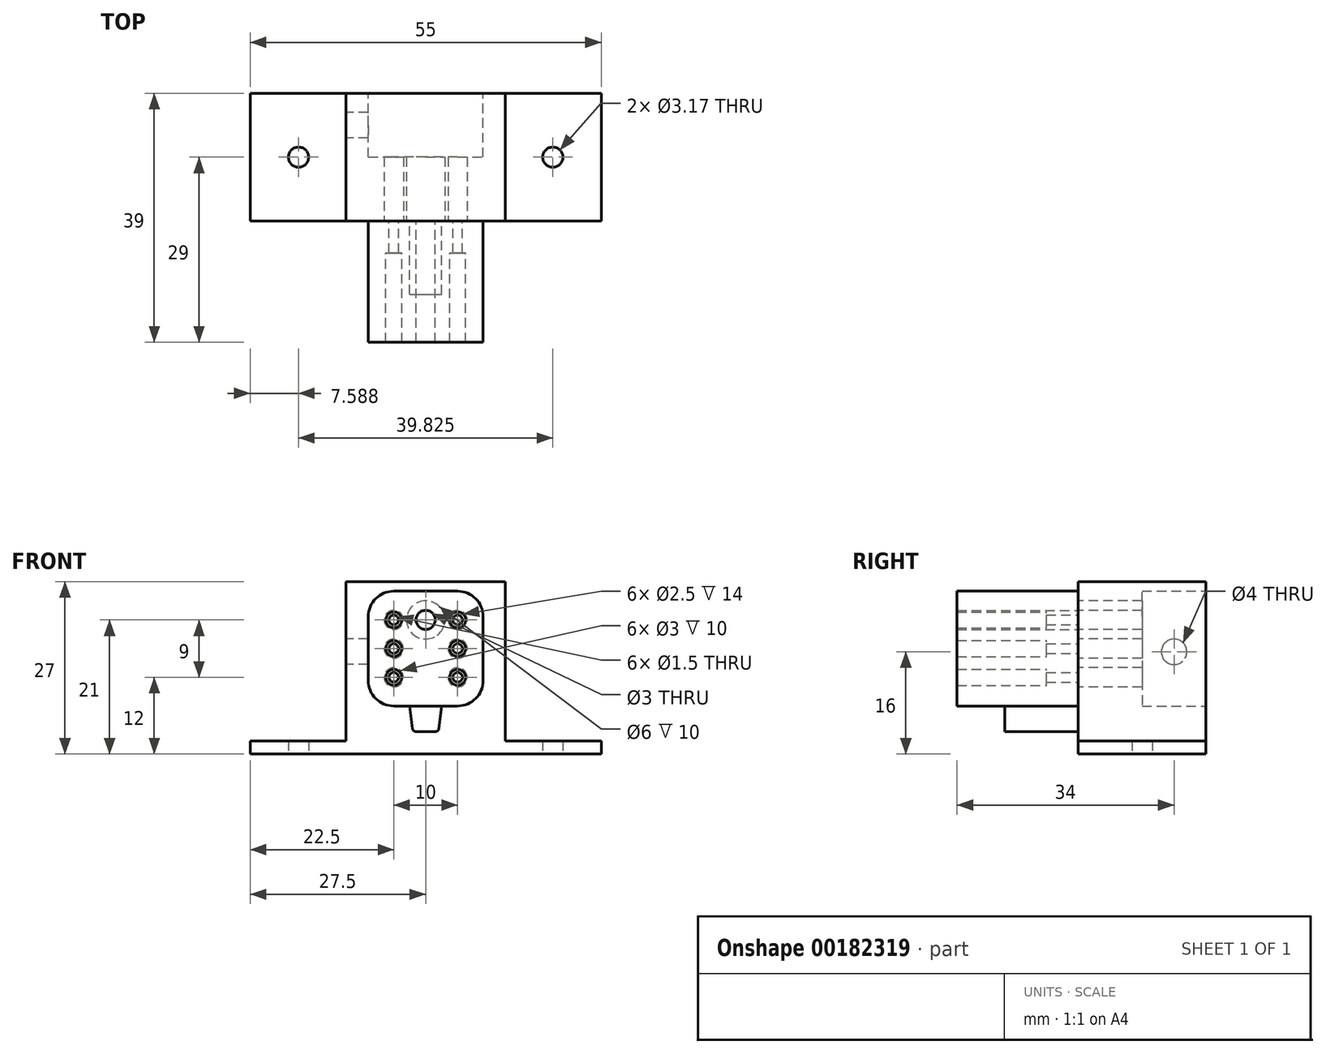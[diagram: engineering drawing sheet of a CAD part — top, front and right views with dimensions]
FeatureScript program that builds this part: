
annotation { "Feature Type Name" : "Feature", "Feature Type Description" : "" }
export const myFeature = defineFeature(function(context is Context, id is Id, definition is map)
    precondition{}
    {
        {
            var Q0;
            Q0=qCreatedBy(makeId("Top.planeOp"),FACE);
            var sketch = newSketch(context, id + "F0", { "sketchPlane" : qUnion([Q0])});
            skLineSegment(sketch, "E0.bottom", {"start": v(0, 0) * mm, "end": v(25, 0) * mm});
            skLineSegment(sketch, "E0.top", {"start": v(0, 20) * mm, "end": v(25, 20) * mm});
            skLineSegment(sketch, "E0.left", {"start": v(0, 0) * mm, "end": v(0, 20) * mm});
            skLineSegment(sketch, "E0.right", {"start": v(25, 0) * mm, "end": v(25, 20) * mm});
            skSolve(sketch);
        }
        {
            var Q0;
            Q0 = qSketchRegion(id + "F0", true);
            extrude(context, id + "F1", {"entities" : qUnion([Q0]), "depth" : 32 * mm});
        }
        {
            var Q0;
            Q0=makeQuery(id+"F1.opExtrude","SWEPT_FACE",FACE,{"disambiguationData":[OSD([sQuery(id+"F0.wireOp",EDGE,"E0.bottom")])]});
            var sketch = newSketch(context, id + "F2", { "sketchPlane" : qUnion([Q0])});
            skLineSegment(sketch, "E1.bottom", {"start": v(7.5, 30.5) * mm, "end": v(17.5, 30.5) * mm});
            skLineSegment(sketch, "E1.top", {"start": v(7.5, 12.5) * mm, "end": v(17.5, 12.5) * mm});
            skLineSegment(sketch, "E1.left", {"start": v(3.5, 26.5) * mm, "end": v(3.5, 16.5) * mm});
            skLineSegment(sketch, "E1.right", {"start": v(21.5, 26.5) * mm, "end": v(21.5, 16.5) * mm});
            skLineSegment(sketch, "E2", {"start": v(3.5, 21.5) * mm, "end": v(0, 21.5) * mm, "construction": true});
            skLineSegment(sketch, "E3", {"start": v(21.5, 21.5) * mm, "end": v(25, 21.5) * mm, "construction": true});
            skPoint(sketch, "E4.visualSharp", {"position": v(3.5, 30.5) * mm});
            skArc(sketch, "E4.filletArc", {"start": v(7.5, 30.5) * mm, "mid": v(4.67, 29.33) * mm, "end": v(3.5, 26.5) * mm});
            skPoint(sketch, "E5.visualSharp", {"position": v(21.5, 30.5) * mm});
            skArc(sketch, "E5.filletArc", {"start": v(21.5, 26.5) * mm, "mid": v(20.33, 29.33) * mm, "end": v(17.5, 30.5) * mm});
            skPoint(sketch, "E6.visualSharp", {"position": v(21.5, 12.5) * mm});
            skArc(sketch, "E6.filletArc", {"start": v(17.5, 12.5) * mm, "mid": v(20.33, 13.67) * mm, "end": v(21.5, 16.5) * mm});
            skPoint(sketch, "E7.visualSharp", {"position": v(3.5, 12.5) * mm});
            skArc(sketch, "E7.filletArc", {"start": v(3.5, 16.5) * mm, "mid": v(4.67, 13.67) * mm, "end": v(7.5, 12.5) * mm});
            skLineSegment(sketch, "E8", {"start": v(12.5, 30.5) * mm, "end": v(12.5, 6.08) * mm, "construction": true});
            skCircle(sketch, "E9", {"center": v(12.5, 26) * mm, "radius": 1.5 * mm});
            skCircle(sketch, "E10", {"center": v(7.5, 26) * mm, "radius": 1.25 * mm});
            skLineSegment(sketch, "E11", {"start": v(7.5, 26) * mm, "end": v(12.5, 26) * mm, "construction": true});
            skCircle(sketch, "E12.1.0.0", {"center": v(7.5, 21.5) * mm, "radius": 1.25 * mm});
            skCircle(sketch, "E12.2.0.0", {"center": v(7.5, 17) * mm, "radius": 1.25 * mm});
            skLineSegment(sketch, "E12.direction1", {"start": v(7.5, 26) * mm, "end": v(7.5, 21.5) * mm, "construction": true});
            skCircle(sketch, "E13.MirrorC", {"center": v(17.5, 26) * mm, "radius": 1.25 * mm});
            skCircle(sketch, "E14.MirrorC", {"center": v(17.5, 21.5) * mm, "radius": 1.25 * mm});
            skCircle(sketch, "E15.MirrorC", {"center": v(17.5, 17) * mm, "radius": 1.25 * mm});
            skLineSegment(sketch, "E16.MirrorCS", {"start": v(17.5, 26) * mm, "end": v(17.5, 21.5) * mm, "construction": true});
            skSolve(sketch);
        }
        {
            var Q0;
            Q0 = qSketchRegion(id + "F2", true);
            extrude(context, id + "F3", {"entities" : qUnion([Q0]), "operationType" : NewBodyOperationType.ADD, "depth" : 19 * mm});
        }
        {
            var Q0;
            Q0=makeQuery(id+"F1.opExtrude","SWEPT_FACE",FACE,{"disambiguationData":[OSD([sQuery(id+"F0.wireOp",EDGE,"E0.top")])]});
            var sketch = newSketch(context, id + "F4", { "sketchPlane" : qUnion([Q0])});
            skLineSegment(sketch, "E17.bottom", {"start": v(-17.5, 30.5) * mm, "end": v(-7.5, 30.5) * mm});
            skLineSegment(sketch, "E17.top", {"start": v(-17.5, 12.5) * mm, "end": v(-7.5, 12.5) * mm});
            skLineSegment(sketch, "E17.left", {"start": v(-21.5, 26.5) * mm, "end": v(-21.5, 16.5) * mm});
            skLineSegment(sketch, "E17.right", {"start": v(-3.5, 26.5) * mm, "end": v(-3.5, 16.5) * mm});
            skLineSegment(sketch, "E18", {"start": v(-21.5, 21.5) * mm, "end": v(-25, 21.5) * mm, "construction": true});
            skLineSegment(sketch, "E19", {"start": v(-3.5, 21.5) * mm, "end": v(0, 21.5) * mm, "construction": true});
            skPoint(sketch, "E20.visualSharp", {"position": v(-21.5, 30.5) * mm});
            skArc(sketch, "E20.filletArc", {"start": v(-17.5, 30.5) * mm, "mid": v(-20.33, 29.33) * mm, "end": v(-21.5, 26.5) * mm});
            skPoint(sketch, "E21.visualSharp", {"position": v(-3.5, 30.5) * mm});
            skArc(sketch, "E21.filletArc", {"start": v(-3.5, 26.5) * mm, "mid": v(-4.67, 29.33) * mm, "end": v(-7.5, 30.5) * mm});
            skPoint(sketch, "E22.visualSharp", {"position": v(-3.5, 12.5) * mm});
            skArc(sketch, "E22.filletArc", {"start": v(-7.5, 12.5) * mm, "mid": v(-4.67, 13.67) * mm, "end": v(-3.5, 16.5) * mm});
            skPoint(sketch, "E23.visualSharp", {"position": v(-21.5, 12.5) * mm});
            skArc(sketch, "E23.filletArc", {"start": v(-21.5, 16.5) * mm, "mid": v(-20.33, 13.67) * mm, "end": v(-17.5, 12.5) * mm});
            skSolve(sketch);
        }
        {
            var Q0;
            Q0 = qSketchRegion(id + "F4", true);
            extrude(context, id + "F5", {"entities" : qUnion([Q0]), "operationType" : NewBodyOperationType.REMOVE, "oppositeDirection" : true, "depth" : 10 * mm});
        }
        {
            var Q0;
            Q0=makeQuery(id+"F1.opExtrude","SWEPT_FACE",FACE,{"disambiguationData":[OSD([sQuery(id+"F0.wireOp",EDGE,"E0.bottom")])]});
            var sketch = newSketch(context, id + "F6", { "sketchPlane" : qUnion([Q0])});
            skLineSegment(sketch, "E24.bottom", {"start": v(10, 12.5) * mm, "end": v(15, 12.5) * mm});
            skPoint(sketch, "E25", {"position": v(12.5, 12.5) * mm});
            skLineSegment(sketch, "E26", {"start": v(10, 12.5) * mm, "end": v(10.45, 8.94) * mm});
            skLineSegment(sketch, "E27", {"start": v(10.94, 8.5) * mm, "end": v(14.06, 8.5) * mm});
            skLineSegment(sketch, "E28", {"start": v(14.55, 8.94) * mm, "end": v(15, 12.5) * mm});
            skLineSegment(sketch, "E29", {"start": v(12.5, 8.5) * mm, "end": v(12.5, 12.5) * mm, "construction": true});
            skPoint(sketch, "E30.visualSharp", {"position": v(10.5, 8.5) * mm});
            skArc(sketch, "E30.filletArc", {"start": v(10.45, 8.94) * mm, "mid": v(10.61, 8.63) * mm, "end": v(10.94, 8.5) * mm});
            skPoint(sketch, "E31.visualSharp", {"position": v(14.5, 8.5) * mm});
            skArc(sketch, "E31.filletArc", {"start": v(14.06, 8.5) * mm, "mid": v(14.39, 8.63) * mm, "end": v(14.55, 8.94) * mm});
            skSolve(sketch);
        }
        {
            var Q0;
            Q0 = qSketchRegion(id + "F6", true);
            extrude(context, id + "F7", {"entities" : qUnion([Q0]), "operationType" : NewBodyOperationType.ADD, "depth" : 11.5 * mm});
        }
        {
            var Q0;
            Q0=makeQuery(id+"F1.opExtrude","SWEPT_FACE",FACE,{"disambiguationData":[OSD([sQuery(id+"F0.wireOp",EDGE,"E0.bottom")])]});
            var sketch = newSketch(context, id + "F8", { "sketchPlane" : qUnion([Q0])});
            skLineSegment(sketch, "E32", {"start": v(12.5, 30.5) * mm, "end": v(12.5, 12.5) * mm, "construction": true});
            skCircle(sketch, "E33", {"center": v(12.5, 26) * mm, "radius": 3 * mm});
            skCircle(sketch, "E34", {"center": v(7.5, 26) * mm, "radius": 1.5 * mm});
            skLineSegment(sketch, "E35", {"start": v(7.5, 26) * mm, "end": v(12.5, 26) * mm, "construction": true});
            skCircle(sketch, "E36.1.0.0", {"center": v(7.5, 21.5) * mm, "radius": 1.5 * mm});
            skCircle(sketch, "E36.2.0.0", {"center": v(7.5, 17) * mm, "radius": 1.5 * mm});
            skLineSegment(sketch, "E36.direction1", {"start": v(7.5, 26) * mm, "end": v(7.5, 21.5) * mm, "construction": true});
            skCircle(sketch, "E37.MirrorC", {"center": v(17.5, 26) * mm, "radius": 1.5 * mm});
            skCircle(sketch, "E38.MirrorC", {"center": v(17.5, 21.5) * mm, "radius": 1.5 * mm});
            skCircle(sketch, "E39.MirrorC", {"center": v(17.5, 17) * mm, "radius": 1.5 * mm});
            skLineSegment(sketch, "E40.MirrorCS", {"start": v(17.5, 26) * mm, "end": v(17.5, 21.5) * mm, "construction": true});
            skSolve(sketch);
        }
        {
            var Q0;
            Q0 = qSketchRegion(id + "F8", true);
            extrude(context, id + "F9", {"entities" : qUnion([Q0]), "operationType" : NewBodyOperationType.REMOVE, "endBound" : BoundingType.THROUGH_ALL, "oppositeDirection" : true, "depth" : 25 * mm});
        }
        {
            var Q0;
            Q0=makeQuery(id+"F1.opExtrude","SWEPT_FACE",FACE,{"disambiguationData":[OSD([sQuery(id+"F0.wireOp",EDGE,"E0.bottom")])]});
            var sketch = newSketch(context, id + "F10", { "sketchPlane" : qUnion([Q0])});
            skLineSegment(sketch, "E41", {"start": v(12.5, 33.14) * mm, "end": v(12.5, 12.56) * mm, "construction": true});
            skCircle(sketch, "E42", {"center": v(7.5, 26) * mm, "radius": 0.75 * mm});
            skLineSegment(sketch, "E43", {"start": v(7.5, 26) * mm, "end": v(12.5, 26) * mm, "construction": true});
            skCircle(sketch, "E44.1.0.0", {"center": v(7.5, 21.5) * mm, "radius": 0.75 * mm});
            skCircle(sketch, "E44.2.0.0", {"center": v(7.5, 17) * mm, "radius": 0.75 * mm});
            skLineSegment(sketch, "E44.direction1", {"start": v(7.5, 26) * mm, "end": v(7.5, 21.5) * mm, "construction": true});
            skCircle(sketch, "E45.MirrorC", {"center": v(17.5, 26) * mm, "radius": 0.75 * mm});
            skCircle(sketch, "E46.MirrorC", {"center": v(17.5, 21.5) * mm, "radius": 0.75 * mm});
            skCircle(sketch, "E47.MirrorC", {"center": v(17.5, 17) * mm, "radius": 0.75 * mm});
            skLineSegment(sketch, "E48.MirrorCS", {"start": v(17.5, 26) * mm, "end": v(17.5, 21.5) * mm, "construction": true});
            skCircle(sketch, "E49", {"center": v(7.5, 26) * mm, "radius": 1.25 * mm});
            skCircle(sketch, "E50.1.0.0", {"center": v(7.5, 21.5) * mm, "radius": 1.25 * mm});
            skCircle(sketch, "E50.2.0.0", {"center": v(7.5, 17) * mm, "radius": 1.25 * mm});
            skCircle(sketch, "E51.MirrorC", {"center": v(17.5, 26) * mm, "radius": 1.25 * mm});
            skCircle(sketch, "E52.MirrorC", {"center": v(17.5, 21.5) * mm, "radius": 1.25 * mm});
            skCircle(sketch, "E53.MirrorC", {"center": v(17.5, 17) * mm, "radius": 1.25 * mm});
            skSolve(sketch);
        }
        {
            var Q0;
            Q0 = qSketchRegion(id + "F10", true);
            extrude(context, id + "F11", {"entities" : qUnion([Q0]), "operationType" : NewBodyOperationType.ADD, "depth" : 5 * mm});
        }
        {
            var Q0;
            Q0=makeQuery(id+"F1.opExtrude","SWEPT_FACE",FACE,{"disambiguationData":[OSD([sQuery(id+"F0.wireOp",EDGE,"E0.left")])]});
            var sketch = newSketch(context, id + "F12", { "sketchPlane" : qUnion([Q0])});
            skCircle(sketch, "E54", {"center": v(-15, 21) * mm, "radius": 2 * mm});
            skSolve(sketch);
        }
        {
            var Q0;
            Q0 = qSketchRegion(id + "F12", true);
            extrude(context, id + "F13", {"entities" : qUnion([Q0]), "operationType" : NewBodyOperationType.REMOVE, "endBound" : BoundingType.UP_TO_NEXT, "oppositeDirection" : true, "depth" : 25 * mm});
        }
        {
            var Q0;
            Q0=makeQuery(id+"F1.opExtrude","SWEPT_FACE",FACE,{"disambiguationData":[OSD([sQuery(id+"F0.wireOp",EDGE,"E0.left")])]});
            var sketch = newSketch(context, id + "F14", { "sketchPlane" : qUnion([Q0])});
            skLineSegment(sketch, "E55.top", {"start": v(-20, 0) * mm, "end": v(0, 0) * mm});
            skLineSegment(sketch, "E55.left", {"start": v(-20, 5) * mm, "end": v(-20, 0) * mm});
            skLineSegment(sketch, "E55.right", {"start": v(0, 5) * mm, "end": v(0, 0) * mm});
            skLineSegment(sketch, "E56.top", {"start": v(-20, 5) * mm, "end": v(0, 5) * mm});
            skSolve(sketch);
        }
        {
            var Q0;
            Q0 = qSketchRegion(id + "F14", true);
            extrude(context, id + "F15", {"entities" : qUnion([Q0]), "operationType" : NewBodyOperationType.REMOVE, "oppositeDirection" : true, "depth" : 25 * mm});
        }
        {
            var Q0;
            Q0=makeQuery(id+"F15.boolean.opBoolean","COPY",FACE,{"derivedFrom":makeQuery(id+"F15.opExtrude","SWEPT_FACE",FACE,{"disambiguationData":[OSD([sQuery(id+"F14.wireOp",EDGE,"E56.top")])]})});
            var sketch = newSketch(context, id + "F16", { "sketchPlane" : qUnion([Q0])});
            skLineSegment(sketch, "E57.bottom", {"start": v(40, 0) * mm, "end": v(-15, 0) * mm});
            skLineSegment(sketch, "E57.top", {"start": v(40, -20) * mm, "end": v(-15, -20) * mm});
            skLineSegment(sketch, "E57.left", {"start": v(40, 0) * mm, "end": v(40, -20) * mm});
            skLineSegment(sketch, "E57.right", {"start": v(-15, 0) * mm, "end": v(-15, -20) * mm});
            skCircle(sketch, "E58", {"center": v(32.41, -10) * mm, "radius": 1.59 * mm});
            skPoint(sketch, "E58.centerSnap0", {"position": v(40, -10) * mm});
            skCircle(sketch, "E59", {"center": v(-7.41, -10) * mm, "radius": 1.59 * mm});
            skPoint(sketch, "E59.centerSnap0", {"position": v(-15, -10) * mm});
            skSolve(sketch);
        }
        {
            var Q0;
            {var subQ0=sQuery(id+"F16.wireOp",EDGE,"E57.left");Q0=makeQuery(id+"F16.imprint","IMPRINT",FACE,{"disambiguationData":[TD([[makeQuery(id+"F16.imprint","IMPRINT",EDGE,{"derivedFrom":subQ0}),-1.0]])]});}
            var Q1;
            {var subQ2=sQuery(id+"F16.wireOp",EDGE,"E57.right");Q1=makeQuery(id+"F16.imprint","IMPRINT",FACE,{"disambiguationData":[TD([[makeQuery(id+"F16.imprint","IMPRINT",EDGE,{"derivedFrom":subQ2}),1.0]])]});}
            extrude(context, id + "F17", {"entities" : qUnion([Q0, Q1]), "operationType" : NewBodyOperationType.ADD, "oppositeDirection" : true, "depth" : 2 * mm});
        }
    });
